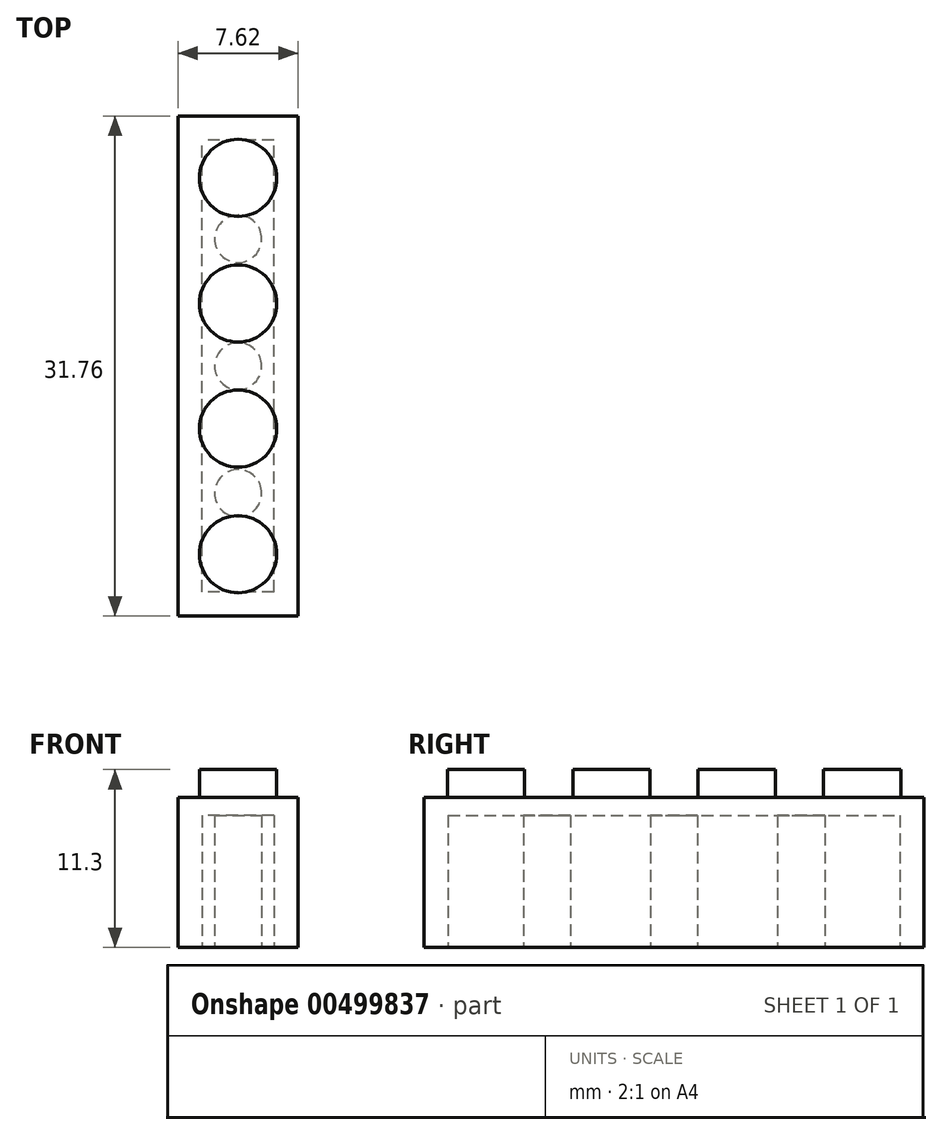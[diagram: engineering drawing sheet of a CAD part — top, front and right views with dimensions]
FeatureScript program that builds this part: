
annotation { "Feature Type Name" : "Feature", "Feature Type Description" : "" }
export const myFeature = defineFeature(function(context is Context, id is Id, definition is map)
    precondition{}
    {
        {
            var Q0;
            Q0=qCreatedBy(makeId("Top.planeOp"),FACE);
            var sketch = newSketch(context, id + "F0", { "sketchPlane" : qUnion([Q0])});
            skLineSegment(sketch, "E0.bottom", {"start": v(3.81, 15.88) * mm, "end": v(-3.8, 15.88) * mm});
            skLineSegment(sketch, "E0.top", {"start": v(3.8, -15.88) * mm, "end": v(-3.81, -15.88) * mm});
            skLineSegment(sketch, "E0.left", {"start": v(3.81, 15.88) * mm, "end": v(3.8, -15.88) * mm});
            skLineSegment(sketch, "E0.right", {"start": v(-3.8, 15.88) * mm, "end": v(-3.81, -15.88) * mm});
            skPoint(sketch, "E0.middle", {"position": v(0, 0) * mm});
            skSolve(sketch);
        }
        {
            var Q0;
            Q0=makeQuery(id+"F0.imprint","IMPRINT",FACE,{"disambiguationData":[TD([[makeQuery(id+"F0.imprint","IMPRINT",EDGE,{"derivedFrom":sQuery(id+"F0.wireOp",EDGE,"E0.bottom")}),1.0]])]});
            extrude(context, id + "F1", {"entities" : qUnion([Q0]), "endBound" : BoundingType.SYMMETRIC, "depth" : 9.52 * mm});
        }
        {
            var Q0;
            Q0=makeQuery(id+"F1.opExtrude","CAP_FACE",FACE,{"disambiguationData":[OSD([sQuery(id+"F0.wireOp",EDGE,"E0.bottom"),sQuery(id+"F0.wireOp",EDGE,"E0.top"),sQuery(id+"F0.wireOp",EDGE,"E0.left"),sQuery(id+"F0.wireOp",EDGE,"E0.right")])],"isStart":false});
            var sketch = newSketch(context, id + "F2", { "sketchPlane" : qUnion([Q0])});
            skCircle(sketch, "E1", {"center": v(0, 11.95) * mm, "radius": 2.45 * mm});
            skCircle(sketch, "E2", {"center": v(0, 3.98) * mm, "radius": 2.45 * mm});
            skCircle(sketch, "E3", {"center": v(0, -3.98) * mm, "radius": 2.45 * mm});
            skCircle(sketch, "E4", {"center": v(0, -11.95) * mm, "radius": 2.45 * mm});
            skSolve(sketch);
        }
        {
            var Q0;
            Q0=makeQuery(id+"F2.imprint","IMPRINT",FACE,{"disambiguationData":[TD([[makeQuery(id+"F2.imprint","IMPRINT",EDGE,{"derivedFrom":sQuery(id+"F2.wireOp",EDGE,"E1")}),1.0]])]});
            var Q1;
            Q1=makeQuery(id+"F2.imprint","IMPRINT",FACE,{"disambiguationData":[TD([[makeQuery(id+"F2.imprint","IMPRINT",EDGE,{"derivedFrom":sQuery(id+"F2.wireOp",EDGE,"E2")}),1.0]])]});
            var Q2;
            Q2=makeQuery(id+"F2.imprint","IMPRINT",FACE,{"disambiguationData":[TD([[makeQuery(id+"F2.imprint","IMPRINT",EDGE,{"derivedFrom":sQuery(id+"F2.wireOp",EDGE,"E3")}),1.0]])]});
            var Q3;
            Q3=makeQuery(id+"F2.imprint","IMPRINT",FACE,{"disambiguationData":[TD([[makeQuery(id+"F2.imprint","IMPRINT",EDGE,{"derivedFrom":sQuery(id+"F2.wireOp",EDGE,"E4")}),1.0]])]});
            extrude(context, id + "F3", {"entities" : qUnion([Q0, Q1, Q2, Q3]), "operationType" : NewBodyOperationType.ADD, "depth" : 1.78 * mm});
        }
        {
            var Q0;
            Q0=makeQuery(id+"F1.opExtrude","CAP_FACE",FACE,{"disambiguationData":[OSD([sQuery(id+"F0.wireOp",EDGE,"E0.bottom"),sQuery(id+"F0.wireOp",EDGE,"E0.top"),sQuery(id+"F0.wireOp",EDGE,"E0.left"),sQuery(id+"F0.wireOp",EDGE,"E0.right")])],"isStart":true});
            var sketch = newSketch(context, id + "F4", { "sketchPlane" : qUnion([Q0])});
            skLineSegment(sketch, "E5.bottom", {"start": v(2.29, 14.35) * mm, "end": v(-2.29, 14.35) * mm});
            skLineSegment(sketch, "E5.top", {"start": v(2.29, -14.35) * mm, "end": v(-2.29, -14.35) * mm});
            skLineSegment(sketch, "E5.left", {"start": v(2.29, 14.35) * mm, "end": v(2.29, -14.35) * mm});
            skLineSegment(sketch, "E5.right", {"start": v(-2.29, 14.35) * mm, "end": v(-2.29, -14.35) * mm});
            skPoint(sketch, "E5.middle", {"position": v(0, 0) * mm});
            skCircle(sketch, "E6", {"center": v(0, 0) * mm, "radius": 1.5 * mm});
            skCircle(sketch, "E7", {"center": v(0, 8.08) * mm, "radius": 1.5 * mm});
            skCircle(sketch, "E8", {"center": v(0, -8.08) * mm, "radius": 1.5 * mm});
            skSolve(sketch);
        }
        {
            var Q0;
            Q0=makeQuery(id+"F4.imprint","IMPRINT",FACE,{"disambiguationData":[TD([[makeQuery(id+"F4.imprint","IMPRINT",EDGE,{"derivedFrom":sQuery(id+"F4.wireOp",EDGE,"E5.bottom")}),1.0]])]});
            extrude(context, id + "F5", {"entities" : qUnion([Q0]), "operationType" : NewBodyOperationType.REMOVE, "oppositeDirection" : true, "depth" : 8.38 * mm});
        }
    });
